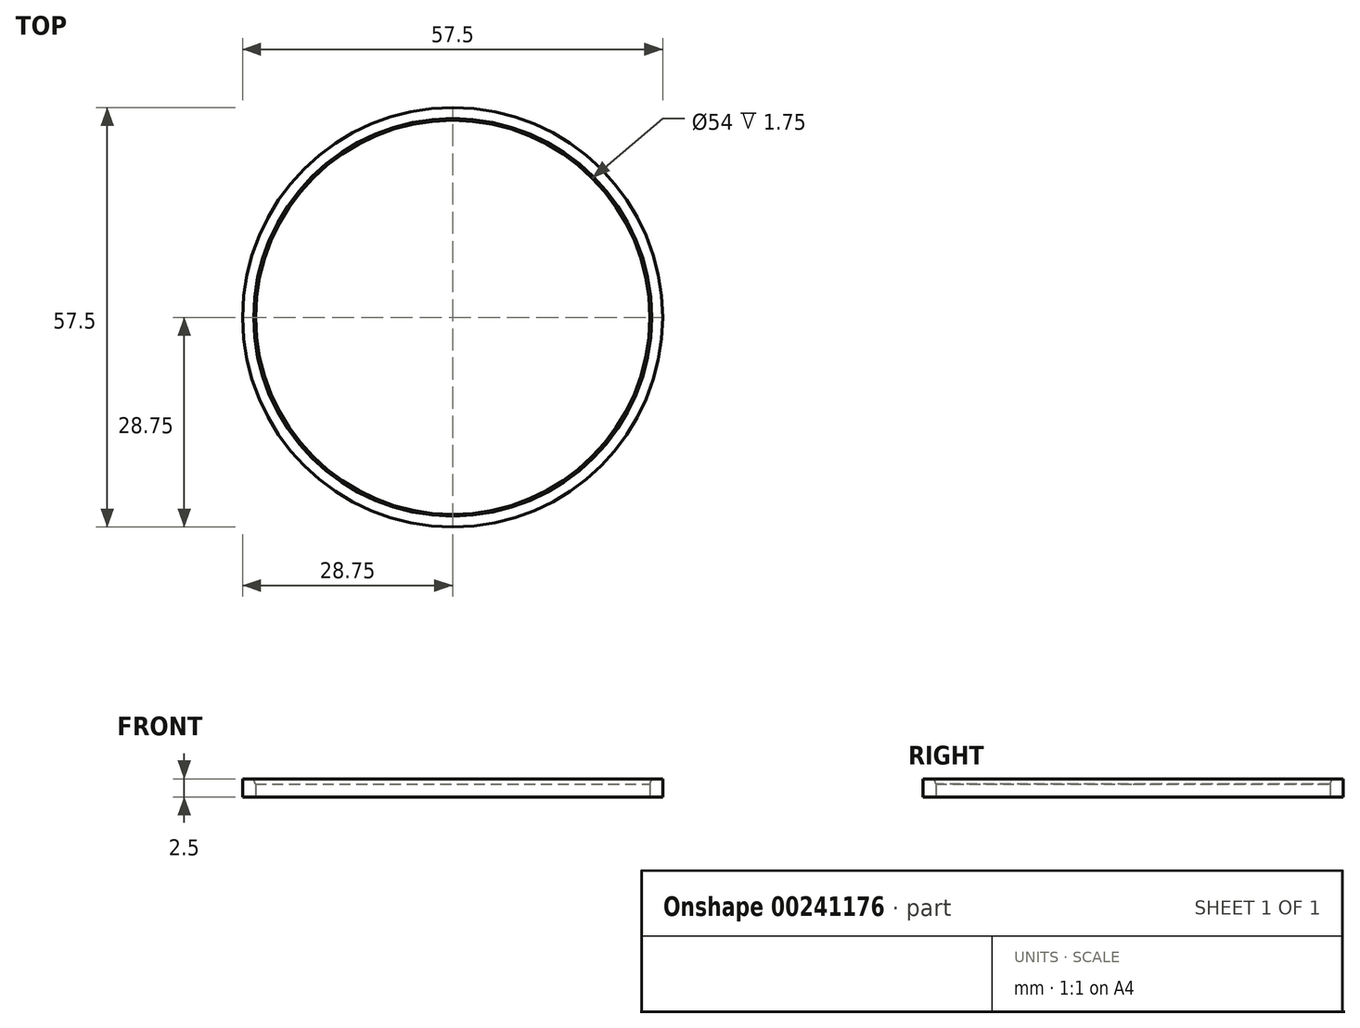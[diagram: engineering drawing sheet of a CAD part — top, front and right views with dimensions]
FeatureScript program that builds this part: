
annotation { "Feature Type Name" : "Feature", "Feature Type Description" : "" }
export const myFeature = defineFeature(function(context is Context, id is Id, definition is map)
    precondition{}
    {
        {
            var Q0;
            Q0=qCreatedBy(makeId("Front.planeOp"),FACE);
            var sketch = newSketch(context, id + "F0", { "sketchPlane" : qUnion([Q0])});
            skLineSegment(sketch, "E0.bottom", {"start": v(27, 0) * mm, "end": v(28.75, 0) * mm});
            skLineSegment(sketch, "E0.top", {"start": v(27.25, 2.5) * mm, "end": v(28.75, 2.5) * mm});
            skLineSegment(sketch, "E0.left", {"start": v(27, 0) * mm, "end": v(27, 1.75) * mm});
            skLineSegment(sketch, "E0.right", {"start": v(28.75, 0) * mm, "end": v(28.75, 2.5) * mm});
            skLineSegment(sketch, "E1", {"start": v(0, 0) * mm, "end": v(0, 19.53) * mm, "construction": true});
            skLineSegment(sketch, "E2", {"start": v(27, 1.75) * mm, "end": v(27.25, 2.5) * mm});
            skSolve(sketch);
        }
        {
            var Q0;
            Q0=makeQuery(id+"F0.imprint","IMPRINT",FACE,{"disambiguationData":[TD([[makeQuery(id+"F0.imprint","IMPRINT",EDGE,{"derivedFrom":sQuery(id+"F0.wireOp",EDGE,"E0.bottom")}),1.0]])]});
            var Q1;
            Q1=sQuery(id+"F0.wireOp",EDGE,"E1");
            revolve(context, id + "F1", {"entities" : qUnion([Q0]), "axis" : qUnion([Q1]), "revolveType" : RevolveType.FULL});
        }
    });
